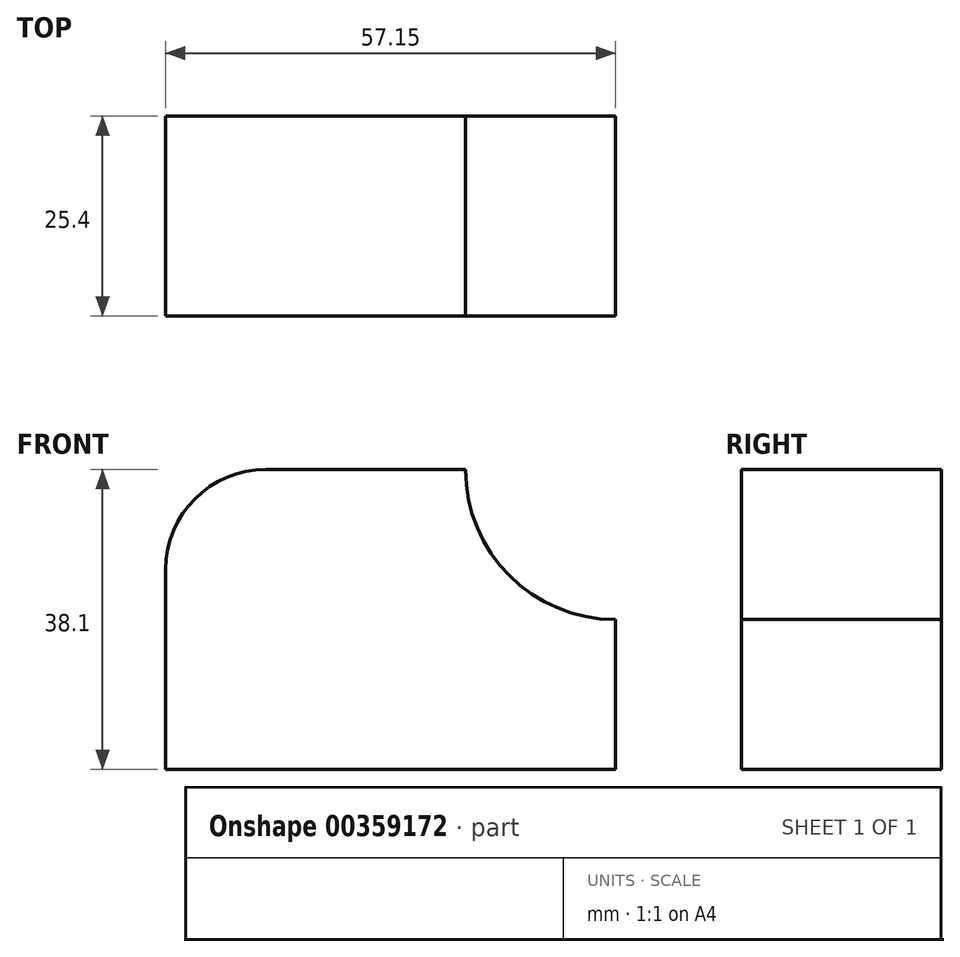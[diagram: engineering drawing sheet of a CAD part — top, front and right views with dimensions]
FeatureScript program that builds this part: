
annotation { "Feature Type Name" : "Feature", "Feature Type Description" : "" }
export const myFeature = defineFeature(function(context is Context, id is Id, definition is map)
    precondition{}
    {
        {
            var Q0;
            Q0=qCreatedBy(makeId("Front.planeOp"),FACE);
            var sketch = newSketch(context, id + "F0", { "sketchPlane" : qUnion([Q0])});
            skLineSegment(sketch, "E0.bottom", {"start": v(-20.76, 30.31) * mm, "end": v(23.69, 30.31) * mm});
            skLineSegment(sketch, "E0.top", {"start": v(-33.46, -7.79) * mm, "end": v(23.69, -7.79) * mm});
            skLineSegment(sketch, "E0.left", {"start": v(-33.46, 17.61) * mm, "end": v(-33.46, -7.79) * mm});
            skLineSegment(sketch, "E0.right", {"start": v(23.69, 30.31) * mm, "end": v(23.69, -7.79) * mm});
            skPoint(sketch, "E1.visualSharp", {"position": v(-33.46, 30.31) * mm});
            skArc(sketch, "E1.filletArc", {"start": v(-20.76, 30.31) * mm, "mid": v(-29.74, 26.6) * mm, "end": v(-33.46, 17.61) * mm});
            skLineSegment(sketch, "E2", {"start": v(4.64, 30.31) * mm, "end": v(4.64, 30.31) * mm});
            skLineSegment(sketch, "E3", {"start": v(23.69, 11.26) * mm, "end": v(23.69, 11.26) * mm});
            skPoint(sketch, "E4.visualSharp", {"position": v(4.64, 11.26) * mm});
            skArc(sketch, "E4.filletArc", {"start": v(4.64, 30.31) * mm, "mid": v(10.22, 16.84) * mm, "end": v(23.69, 11.26) * mm});
            skSolve(sketch);
        }
        {
            var Q0;
            {var subQ0=sQuery(id+"F0.wireOp",EDGE,"E0.top");Q0=makeQuery(id+"F0.imprint","IMPRINT",FACE,{"disambiguationData":[TD([[makeQuery(id+"F0.imprint","IMPRINT",EDGE,{"derivedFrom":subQ0}),1.0]])]});}
            extrude(context, id + "F1", {"entities" : qUnion([Q0]), "depth" : 25.4 * mm});
        }
    });
